# Revit family: 305_79cc9c172e0d4906a7edb21e1ae08e
name_source: partatom
category: Pipe Accessories
revit_build: Autodesk Revit 2018 (Build: 20170223_1515(x64)
units: mm (PartAtom-declared; Revit-internal decimal feet)

## family parameters
Always vertical = Yes
Cut with Voids When Loaded = No
Part Type = Valve - Breaks Into
Round Connector Dimension = Use Diameter
Shared = No
Work Plane-Based = No

## types (2) — shared parameters
CAT0 = Yes
Description = Giacoqest Valve
HD1 = 4 mm  [stored 0.0131234 ft]
L2D_Min = 3048 mm
L6 = 3 mm  [stored 0.00984252 ft]
L6__ve = -3 mm  [stored -0.00984252 ft]
Manufacturer = Giacomini
QmdConnectorList = 301;D;302;D
S3 = 2 mm  [stored 0.00656168 ft]
URL = http://www.giacomini.com
magiPartTypeId = 305
magiProductFamilyId = 79cc9c172e0d4906a7edb21e1ae08e
zero-valued in all types: MC_Default_elevation

## per-type parameters (varying)
- GZ650Y003: B1=36 mm  [stored 0.11811 ft]; C=63 mm; C1=38 mm  [stored 0.124672 ft]; C1__ve=-38 mm; CenSd_H2_6=11 mm; D=15 mm; H2=13 mm  [stored 0.0426509 ft]; H4=9 mm  [stored 0.0295276 ft]; HD2=13 mm  [stored 0.0426509 ft]; I=30 mm  [stored 0.0984252 ft]; J=16 mm  [stored 0.0524934 ft]; J3=13 mm  [stored 0.0426509 ft]; J__ve=-16 mm  [stored -0.0524934 ft]; L2=30 mm  [stored 0.0984252 ft]; L2D=60 mm; L3=11 mm; L3__ve=-11 mm; L4=7 mm  [stored 0.0229659 ft]; L4__ve=-7 mm; L5=12 mm  [stored 0.0393701 ft]; L7=9 mm  [stored 0.0295276 ft]; LL=28 mm; LL__ve=-28 mm; R1=8 mm  [stored 0.0262467 ft]; R2=10 mm  [stored 0.0328084 ft]; S2=4 mm  [stored 0.0131234 ft]; S2__ve=-4 mm  [stored -0.0131234 ft]; S4=6 mm  [stored 0.019685 ft]; W2D=15 mm  [stored 0.0492126 ft]; magiProductId=960d0e8d8dd04f8aa3914076276871
- GZ650Y004: B1=41 mm; C=73 mm; C1=44 mm; C1__ve=-44 mm; CenSd_H2_6=14 mm  [stored 0.0459318 ft]; D=20 mm; H2=16 mm  [stored 0.0524934 ft]; H4=11 mm; HD2=15 mm  [stored 0.0492126 ft]; I=34 mm  [stored 0.111549 ft]; J=21 mm; J3=17 mm; J__ve=-21 mm; L2=34 mm  [stored 0.111549 ft]; L2D=68 mm; L3=12 mm  [stored 0.0393701 ft]; L3__ve=-12 mm  [stored -0.0393701 ft]; L4=8 mm  [stored 0.0262467 ft]; L4__ve=-8 mm  [stored -0.0262467 ft]; L5=14 mm  [stored 0.0459318 ft]; L7=10 mm  [stored 0.0328084 ft]; LL=32 mm  [stored 0.104987 ft]; LL__ve=-32 mm; R1=10 mm  [stored 0.0328084 ft]; R2=12 mm  [stored 0.0393701 ft]; S2=5 mm  [stored 0.0164042 ft]; S2__ve=-5 mm  [stored -0.0164042 ft]; S4=7 mm  [stored 0.0229659 ft]; W2D=20 mm  [stored 0.0656168 ft]; magiProductId=7fd30f095fbc47eaa9bf8908693c7b

note: column(s) folded — value = type name in every type: magiProductCode

note: [stored X ft] marks values corroborated as IEEE doubles in the binary element streams (Revit-internal decimal feet)

## geometry (parser evidence)
native form markers: Sweep x1
no freeform markers — native parametric forms only
